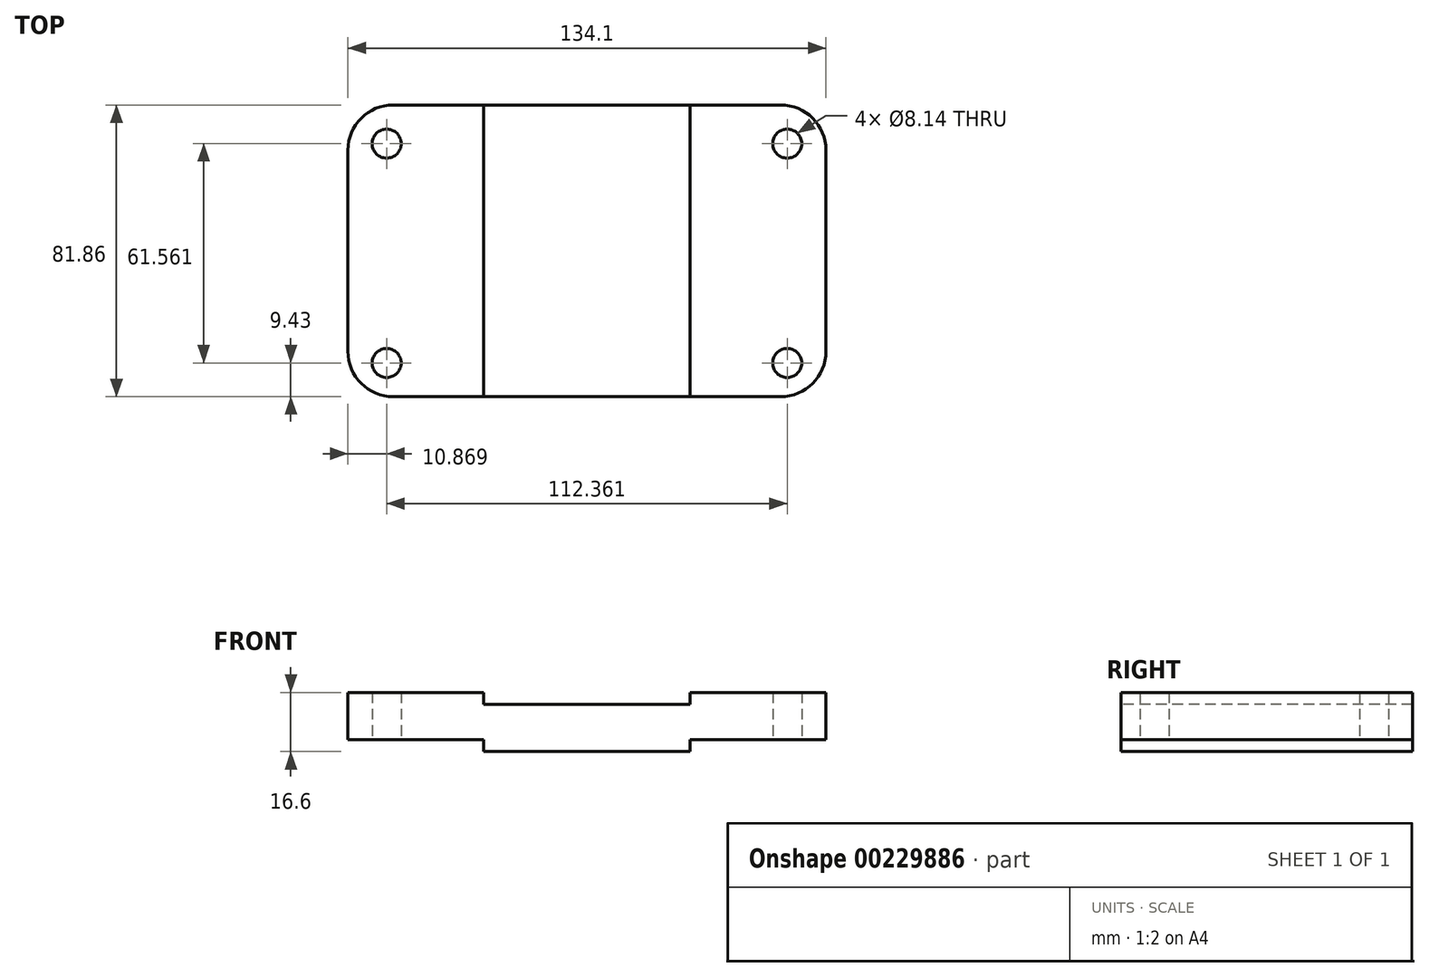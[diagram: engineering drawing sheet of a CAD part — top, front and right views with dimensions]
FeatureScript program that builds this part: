
annotation { "Feature Type Name" : "Feature", "Feature Type Description" : "" }
export const myFeature = defineFeature(function(context is Context, id is Id, definition is map)
    precondition{}
    {
        {
            var Q0;
            Q0=qCreatedBy(makeId("Top.planeOp"),FACE);
            var sketch = newSketch(context, id + "F0", { "sketchPlane" : qUnion([Q0])});
            skLineSegment(sketch, "E0.bottom", {"start": v(67.05, -40.93) * mm, "end": v(-67.05, -40.93) * mm});
            skLineSegment(sketch, "E0.top", {"start": v(67.05, 40.93) * mm, "end": v(-67.05, 40.93) * mm});
            skLineSegment(sketch, "E0.left", {"start": v(67.05, -40.93) * mm, "end": v(67.05, 40.93) * mm});
            skLineSegment(sketch, "E0.right", {"start": v(-67.05, -40.93) * mm, "end": v(-67.05, 40.93) * mm});
            skPoint(sketch, "E0.middle", {"position": v(0, 0) * mm});
            skLineSegment(sketch, "E1", {"start": v(-28.95, 40.93) * mm, "end": v(-28.95, -40.93) * mm});
            skLineSegment(sketch, "E2", {"start": v(28.95, 40.93) * mm, "end": v(28.95, -40.93) * mm});
            skCircle(sketch, "E3", {"center": v(-56.18, 30.06) * mm, "radius": 4.07 * mm});
            skCircle(sketch, "E4", {"center": v(-56.18, -31.5) * mm, "radius": 4.07 * mm});
            skLineSegment(sketch, "E5", {"start": v(-56.18, 34.13) * mm, "end": v(-56.18, -35.57) * mm, "construction": true});
            skLineSegment(sketch, "E6", {"start": v(-56.18, 30.06) * mm, "end": v(-60.25, 30.06) * mm, "construction": true});
            skLineSegment(sketch, "E7", {"start": v(0, 40.93) * mm, "end": v(0, -40.93) * mm});
            skLineSegment(sketch, "E8", {"start": v(-56.18, -31.5) * mm, "end": v(-60.25, -31.5) * mm, "construction": true});
            skLineSegment(sketch, "E9.MirrorCS", {"start": v(56.18, 34.13) * mm, "end": v(56.18, -35.57) * mm, "construction": true});
            skCircle(sketch, "E10.MirrorC", {"center": v(56.18, -31.5) * mm, "radius": 4.07 * mm});
            skCircle(sketch, "E11.MirrorC", {"center": v(56.18, 30.06) * mm, "radius": 4.07 * mm});
            skSolve(sketch);
        }
        {
            var Q0;
            {var subQ1=sQuery(id+"F0.wireOp",EDGE,"E0.right");Q0=makeQuery(id+"F0.imprint","IMPRINT",FACE,{"disambiguationData":[TD([[makeQuery(id+"F0.imprint","IMPRINT",EDGE,{"derivedFrom":subQ1}),-1.0]])]});}
            var Q1;
            {var subQ1=sQuery(id+"F0.wireOp",EDGE,"E0.left");Q1=makeQuery(id+"F0.imprint","IMPRINT",FACE,{"disambiguationData":[TD([[makeQuery(id+"F0.imprint","IMPRINT",EDGE,{"derivedFrom":subQ1}),1.0]])]});}
            extrude(context, id + "F1", {"entities" : qUnion([Q0, Q1]), "depth" : 13.3 * mm});
        }
        {
            var Q0;
            {var subQ0=sQuery(id+"F0.wireOp",EDGE,"E2");Q0=makeQuery(id+"F0.imprint","IMPRINT",FACE,{"disambiguationData":[TD([[makeQuery(id+"F0.imprint","IMPRINT",EDGE,{"derivedFrom":subQ0}),-1.0]])]});}
            var Q1;
            {var subQ0=sQuery(id+"F0.wireOp",EDGE,"E1");Q1=makeQuery(id+"F0.imprint","IMPRINT",FACE,{"disambiguationData":[TD([[makeQuery(id+"F0.imprint","IMPRINT",EDGE,{"derivedFrom":subQ0}),1.0]])]});}
            extrude(context, id + "F2", {"entities" : qUnion([Q0, Q1]), "depth" : 10 * mm});
        }
        {
            var Q0;
            Q0=makeQuery(id+"F2.opExtrude","CAP_FACE",FACE,{"disambiguationData":[OSD([sQuery(id+"F0.wireOp",EDGE,"E0.bottom"),sQuery(id+"F0.wireOp",EDGE,"E0.top"),sQuery(id+"F0.wireOp",EDGE,"E1"),sQuery(id+"F0.wireOp",EDGE,"E2")])],"isStart":true});
            var sketch = newSketch(context, id + "F3", { "sketchPlane" : qUnion([Q0])});
            skLineSegment(sketch, "E12.bottom", {"start": v(-28.95, 40.93) * mm, "end": v(28.95, 40.93) * mm});
            skLineSegment(sketch, "E12.top", {"start": v(-28.95, -40.93) * mm, "end": v(28.95, -40.93) * mm});
            skLineSegment(sketch, "E12.left", {"start": v(-28.95, 40.93) * mm, "end": v(-28.95, -40.93) * mm});
            skLineSegment(sketch, "E12.right", {"start": v(28.95, 40.93) * mm, "end": v(28.95, -40.93) * mm});
            skSolve(sketch);
        }
        {
            var Q0;
            Q0=makeQuery(id+"F3.imprint","IMPRINT",FACE,{"disambiguationData":[TD([[makeQuery(id+"F3.imprint","IMPRINT",EDGE,{"derivedFrom":sQuery(id+"F3.wireOp",EDGE,"E12.bottom")}),1.0]])]});
            extrude(context, id + "F4", {"entities" : qUnion([Q0]), "operationType" : NewBodyOperationType.ADD, "depth" : 3.3 * mm});
        }
        {
            var Q0;
            Q0=makeQuery(id+"F1.opExtrude","SWEPT_EDGE",EDGE,{"disambiguationData":[OSD([sQuery(id+"F0.wireOp",EDGE,"E0.bottom"),sQuery(id+"F0.wireOp",EDGE,"E0.left")])]});
            var Q1;
            Q1=makeQuery(id+"F1.opExtrude","SWEPT_EDGE",EDGE,{"disambiguationData":[OSD([sQuery(id+"F0.wireOp",EDGE,"E0.top"),sQuery(id+"F0.wireOp",EDGE,"E0.left")])]});
            var Q2;
            Q2=makeQuery(id+"F1.opExtrude","SWEPT_EDGE",EDGE,{"disambiguationData":[OSD([sQuery(id+"F0.wireOp",EDGE,"E0.top"),sQuery(id+"F0.wireOp",EDGE,"E0.right")])]});
            var Q3;
            Q3=makeQuery(id+"F1.opExtrude","SWEPT_EDGE",EDGE,{"disambiguationData":[OSD([sQuery(id+"F0.wireOp",EDGE,"E0.bottom"),sQuery(id+"F0.wireOp",EDGE,"E0.right")])]});
            fillet(context, id + "F5", {"entities" : qUnion([Q0, Q1, Q2, Q3]), "radius" : 12.7 * mm, "tangentPropagation" : true, "allowEdgeOverflow" : false});
        }
    });
